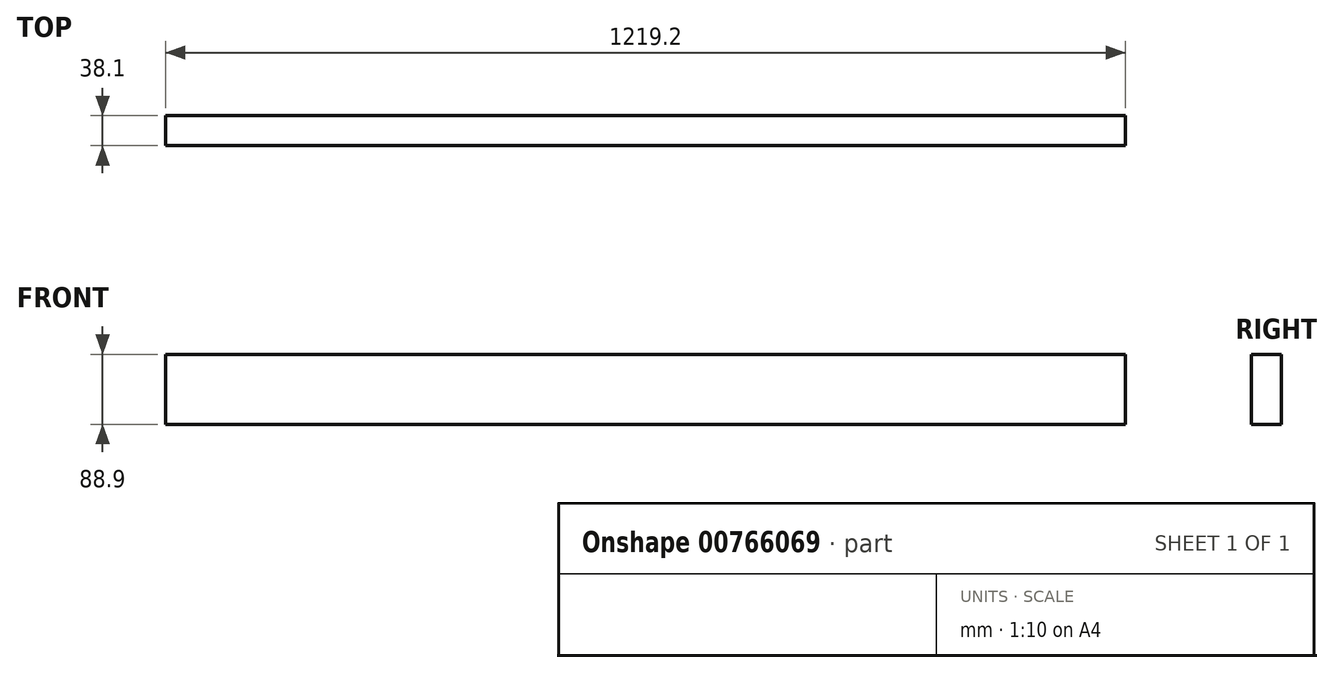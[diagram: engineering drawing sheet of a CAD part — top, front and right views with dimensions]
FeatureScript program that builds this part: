
annotation { "Feature Type Name" : "Feature", "Feature Type Description" : "" }
export const myFeature = defineFeature(function(context is Context, id is Id, definition is map)
    precondition{}
    {
        {
            var Q0;
            Q0=qCreatedBy(makeId("Front.planeOp"),FACE);
            var sketch = newSketch(context, id + "F0", { "sketchPlane" : qUnion([Q0])});
            skLineSegment(sketch, "E0.bottom", {"start": v(-609.6, 0) * mm, "end": v(609.6, 0) * mm});
            skLineSegment(sketch, "E0.top", {"start": v(-609.6, -88.9) * mm, "end": v(609.6, -88.9) * mm});
            skLineSegment(sketch, "E0.left", {"start": v(-609.6, 0) * mm, "end": v(-609.6, -88.9) * mm});
            skLineSegment(sketch, "E0.right", {"start": v(609.6, 0) * mm, "end": v(609.6, -88.9) * mm});
            skSolve(sketch);
        }
        {
            var Q0;
            Q0=qSketchRegion(id+"F0",true);
            extrude(context, id + "F1", {"entities" : qUnion([Q0]), "depth" : 38.1 * mm, "offsetDistance" : 25.4 * mm});
        }
    });
